FCSTD DOCUMENT  (FreeCAD 0.18R4 (GitTag))
Label: butelka bok
License: All rights reserved
LicenseURL: http://en.wikipedia.org/wiki/All_rights_reserved
objects: Sketcher::SketchObject×2, PartDesign::Body×1, Part::MultiFuse×1
note: 4 computed .brp shape members not serialized (recipe doc carries the construction recipe); baked Part::Feature solids carry a one-line shape summary decoded from their .brp

FEATURE [Sketcher::SketchObject] Sketch001
  AttachmentOffset = pos=(0,0,0) rot=(0,0,1;-0.331801rad)
  MapMode = 5
  Placement = pos=(0,0,0) rot=(0,0,1;5.95138rad)
  Support = -> [XY_Plane]
  sketch-geometry (153):
    g0: LineSegment StartX=0 StartY=0 StartZ=0 EndX=0 EndY=25 EndZ=0
    g1: LineSegment StartX=0 StartY=25 StartZ=0 EndX=-3.65 EndY=25 EndZ=0
    g2: LineSegment StartX=-3.65 StartY=25 StartZ=0 EndX=-3.65 EndY=28 EndZ=0
    g3: LineSegment StartX=-3.65 StartY=28 StartZ=0 EndX=0 EndY=28 EndZ=0
    g4: LineSegment StartX=0 StartY=28 StartZ=0 EndX=0 EndY=31 EndZ=0
    g5: LineSegment StartX=0 StartY=31 StartZ=0 EndX=-3.65 EndY=31 EndZ=0
    g6: LineSegment StartX=-3.65 StartY=31 StartZ=0 EndX=-3.65 EndY=34 EndZ=0
    g7: LineSegment StartX=-3.65 StartY=34 StartZ=0 EndX=0 EndY=34 EndZ=0
    g8: LineSegment StartX=0 StartY=34 StartZ=0 EndX=0 EndY=37 EndZ=0
    g9: LineSegment StartX=0 StartY=37 StartZ=0 EndX=-3.65 EndY=37 EndZ=0
    g10: LineSegment StartX=-3.65 StartY=37 StartZ=0 EndX=-3.65 EndY=40 EndZ=0
    g11: LineSegment StartX=-3.65 StartY=40 StartZ=0 EndX=0 EndY=40 EndZ=0
    g12: LineSegment StartX=0 StartY=40 StartZ=0 EndX=0 EndY=43 EndZ=0
    g13: LineSegment StartX=0 StartY=43 StartZ=0 EndX=-3.65 EndY=43 EndZ=0
    g14: LineSegment StartX=-3.65 StartY=43 StartZ=0 EndX=-3.65 EndY=46 EndZ=0
    g15: LineSegment StartX=-3.65 StartY=46 StartZ=0 EndX=0 EndY=46 EndZ=0
    g16: LineSegment StartX=0 StartY=46 StartZ=0 EndX=0 EndY=49 EndZ=0
    g17: LineSegment StartX=0 StartY=49 StartZ=0 EndX=-3.65 EndY=49 EndZ=0
    g18: LineSegment StartX=-3.65 StartY=49 StartZ=0 EndX=-3.65 EndY=52 EndZ=0
    g19: LineSegment StartX=-3.65 StartY=52 StartZ=0 EndX=0 EndY=52 EndZ=0
    g20: LineSegment StartX=0 StartY=52 StartZ=0 EndX=0 EndY=55 EndZ=0
    g21: LineSegment StartX=0 StartY=55 StartZ=0 EndX=-3.65 EndY=55 EndZ=0
    g22: LineSegment StartX=-3.65 StartY=55 StartZ=0 EndX=-3.65 EndY=58 EndZ=0
    g23: LineSegment StartX=-3.65 StartY=58 StartZ=0 EndX=0 EndY=58 EndZ=0
    g24: LineSegment StartX=0 StartY=58 StartZ=0 EndX=0 EndY=61 EndZ=0
    g25: LineSegment StartX=0 StartY=61 StartZ=0 EndX=-3.65 EndY=61 EndZ=0
    g26: LineSegment StartX=-3.65 StartY=61 StartZ=0 EndX=-3.65 EndY=64 EndZ=0
    g27: LineSegment StartX=-3.65 StartY=64 StartZ=0 EndX=0 EndY=64 EndZ=0
    g28: LineSegment StartX=0 StartY=64 StartZ=0 EndX=0 EndY=67 EndZ=0
    g29: LineSegment StartX=0 StartY=67 StartZ=0 EndX=-3.65 EndY=67 EndZ=0
    g30: LineSegment StartX=-3.65 StartY=67 StartZ=0 EndX=-3.65 EndY=70 EndZ=0
    g31: LineSegment StartX=-3.65 StartY=70 StartZ=0 EndX=0 EndY=70 EndZ=0
    g32: LineSegment StartX=0 StartY=70 StartZ=0 EndX=0 EndY=73 EndZ=0
    g33: LineSegment StartX=0 StartY=73 StartZ=0 EndX=-3.65 EndY=73 EndZ=0
    g34: LineSegment StartX=-3.65 StartY=73 StartZ=0 EndX=-3.65 EndY=76 EndZ=0
    g35: LineSegment StartX=-3.65 StartY=76 StartZ=0 EndX=0 EndY=76 EndZ=0
    g36: LineSegment StartX=0 StartY=76 StartZ=0 EndX=0 EndY=79 EndZ=0
    g37: LineSegment StartX=0 StartY=79 StartZ=0 EndX=-3.65 EndY=79 EndZ=0
    g38: LineSegment StartX=-3.65 StartY=79 StartZ=0 EndX=-3.65 EndY=82 EndZ=0
    g39: LineSegment StartX=-3.65 StartY=82 StartZ=0 EndX=0 EndY=82 EndZ=0
    g40: LineSegment StartX=0 StartY=82 StartZ=0 EndX=0 EndY=85 EndZ=0
    g41: LineSegment StartX=0 StartY=85 StartZ=0 EndX=-3.65 EndY=85 EndZ=0
    g42: LineSegment StartX=-3.65 StartY=85 StartZ=0 EndX=-3.65 EndY=88 EndZ=0
    g43: LineSegment StartX=-3.65 StartY=88 StartZ=0 EndX=0 EndY=88 EndZ=0
    g44: LineSegment StartX=0 StartY=88 StartZ=0 EndX=0 EndY=91 EndZ=0
    g45: LineSegment StartX=0 StartY=91 StartZ=0 EndX=-3.65 EndY=91 EndZ=0
    g46: LineSegment StartX=-3.65 StartY=91 StartZ=0 EndX=-3.65 EndY=94 EndZ=0
    g47: LineSegment StartX=-3.65 StartY=94 StartZ=0 EndX=0 EndY=94 EndZ=0
    g48: LineSegment StartX=0 StartY=94 StartZ=0 EndX=0 EndY=97 EndZ=0
    g49: LineSegment StartX=0 StartY=97 StartZ=0 EndX=-3.65 EndY=97 EndZ=0
    g50: LineSegment StartX=-3.65 StartY=97 StartZ=0 EndX=-3.65 EndY=100 EndZ=0
    g51: LineSegment StartX=-3.65 StartY=100 StartZ=0 EndX=0 EndY=100 EndZ=0
    g52: LineSegment StartX=0 StartY=100 StartZ=0 EndX=0 EndY=103 EndZ=0
    g53: LineSegment StartX=0 StartY=103 StartZ=0 EndX=-3.65 EndY=103 EndZ=0
    g54: LineSegment StartX=-3.65 StartY=103 StartZ=0 EndX=-3.65 EndY=106 EndZ=0
    g55: LineSegment StartX=-3.65 StartY=106 StartZ=0 EndX=0 EndY=106 EndZ=0
    g56: LineSegment StartX=0 StartY=106 StartZ=0 EndX=0 EndY=109 EndZ=0
    g57: LineSegment StartX=0 StartY=109 StartZ=0 EndX=-3.65 EndY=109 EndZ=0
    g58: LineSegment StartX=-3.65 StartY=109 StartZ=0 EndX=-3.65 EndY=112 EndZ=0
    g59: LineSegment StartX=-3.65 StartY=112 StartZ=0 EndX=0 EndY=112 EndZ=0
    g60: LineSegment StartX=0 StartY=112 StartZ=0 EndX=0 EndY=115 EndZ=0
    g61: LineSegment StartX=0 StartY=115 StartZ=0 EndX=-3.65 EndY=115 EndZ=0
    g62: LineSegment StartX=-3.65 StartY=115 StartZ=0 EndX=-3.65 EndY=118 EndZ=0
    g63: LineSegment StartX=-3.65 StartY=118 StartZ=0 EndX=0 EndY=118 EndZ=0
    g64: LineSegment StartX=0 StartY=118 StartZ=0 EndX=0 EndY=121 EndZ=0
    g65: LineSegment StartX=0 StartY=121 StartZ=0 EndX=-3.65 EndY=121 EndZ=0
    g66: LineSegment StartX=-3.65 StartY=121 StartZ=0 EndX=-3.65 EndY=124 EndZ=0
    g67: LineSegment StartX=-3.65 StartY=124 StartZ=0 EndX=0 EndY=124 EndZ=0
    g68: LineSegment StartX=0 StartY=124 StartZ=0 EndX=0 EndY=127 EndZ=0
    g69: LineSegment StartX=0 StartY=127 StartZ=0 EndX=-3.65 EndY=127 EndZ=0
    g70: LineSegment StartX=-3.65 StartY=127 StartZ=0 EndX=-3.65 EndY=130 EndZ=0
    g71: LineSegment StartX=-3.65 StartY=130 StartZ=0 EndX=0 EndY=130 EndZ=0
    g72: LineSegment StartX=0 StartY=130 StartZ=0 EndX=0 EndY=133 EndZ=0
    g73: LineSegment StartX=0 StartY=133 StartZ=0 EndX=-3.65 EndY=133 EndZ=0
    g74: LineSegment StartX=-3.65 StartY=133 StartZ=0 EndX=-3.65 EndY=136 EndZ=0
    g75: LineSegment StartX=-3.65 StartY=136 StartZ=0 EndX=0 EndY=136 EndZ=0
    g76: LineSegment StartX=0 StartY=136 StartZ=0 EndX=0 EndY=139 EndZ=0
    g77: LineSegment StartX=0 StartY=139 StartZ=0 EndX=-3.65 EndY=139 EndZ=0
    g78: LineSegment StartX=-3.65 StartY=139 StartZ=0 EndX=-3.65 EndY=142 EndZ=0
    g79: LineSegment StartX=-3.65 StartY=142 StartZ=0 EndX=0 EndY=142 EndZ=0
    g80: LineSegment StartX=0 StartY=142 StartZ=0 EndX=0 EndY=145 EndZ=0
    g81: LineSegment StartX=0 StartY=145 StartZ=0 EndX=-3.65 EndY=145 EndZ=0
    g82: LineSegment StartX=-3.65 StartY=145 StartZ=0 EndX=-3.65 EndY=148 EndZ=0
    g83: LineSegment StartX=-3.65 StartY=148 StartZ=0 EndX=0 EndY=148 EndZ=0
    g84: LineSegment StartX=0 StartY=148 StartZ=0 EndX=0 EndY=151 EndZ=0
    g85: LineSegment StartX=0 StartY=151 StartZ=0 EndX=-3.65 EndY=151 EndZ=0
    g86: LineSegment StartX=-3.65 StartY=151 StartZ=0 EndX=-3.65 EndY=154 EndZ=0
    g87: LineSegment StartX=-3.65 StartY=154 StartZ=0 EndX=0 EndY=154 EndZ=0
    g88: LineSegment StartX=0 StartY=154 StartZ=0 EndX=0 EndY=157 EndZ=0
    g89: LineSegment StartX=0 StartY=157 StartZ=0 EndX=-3.65 EndY=157 EndZ=0
    g90: LineSegment StartX=-3.65 StartY=157 StartZ=0 EndX=-3.65 EndY=160 EndZ=0
    g91: LineSegment StartX=-3.65 StartY=160 StartZ=0 EndX=0 EndY=160 EndZ=0
    g92: LineSegment StartX=0 StartY=160 StartZ=0 EndX=0 EndY=163 EndZ=0
    g93: LineSegment StartX=0 StartY=163 StartZ=0 EndX=-3.65 EndY=163 EndZ=0
    g94: LineSegment StartX=-3.65 StartY=163 StartZ=0 EndX=-3.65 EndY=166 EndZ=0
    g95: LineSegment StartX=-3.65 StartY=166 StartZ=0 EndX=0 EndY=166 EndZ=0
    g96: LineSegment StartX=0 StartY=166 StartZ=0 EndX=0 EndY=169 EndZ=0
    g97: LineSegment StartX=0 StartY=169 StartZ=0 EndX=-3.65 EndY=169 EndZ=0
    g98: LineSegment StartX=-3.65 StartY=169 StartZ=0 EndX=-3.65 EndY=172 EndZ=0
    g99: LineSegment StartX=-3.65 StartY=172 StartZ=0 EndX=0 EndY=172 EndZ=0
    g100: LineSegment StartX=0 StartY=172 StartZ=0 EndX=0 EndY=175 EndZ=0
    g101: LineSegment StartX=0 StartY=175 StartZ=0 EndX=-3.65 EndY=175 EndZ=0
    g102: LineSegment StartX=-3.65 StartY=175 StartZ=0 EndX=-3.65 EndY=178 EndZ=0
    g103: LineSegment StartX=-3.65 StartY=178 StartZ=0 EndX=0 EndY=178 EndZ=0
    g104: LineSegment StartX=0 StartY=178 StartZ=0 EndX=0 EndY=181 EndZ=0
    g105: LineSegment StartX=0 StartY=181 StartZ=0 EndX=-3.65 EndY=181 EndZ=0
    g106: LineSegment StartX=-3.65 StartY=181 StartZ=0 EndX=-3.65 EndY=184 EndZ=0
    g107: LineSegment StartX=-3.65 StartY=184 StartZ=0 EndX=0 EndY=184 EndZ=0
    g108: LineSegment StartX=0 StartY=184 StartZ=0 EndX=0 EndY=187 EndZ=0
    g109: LineSegment StartX=0 StartY=187 StartZ=0 EndX=-3.65 EndY=187 EndZ=0
    g110: LineSegment StartX=-3.65 StartY=187 StartZ=0 EndX=-3.65 EndY=190 EndZ=0
    g111: LineSegment StartX=-3.65 StartY=190 StartZ=0 EndX=0 EndY=190 EndZ=0
    g112: LineSegment StartX=0 StartY=190 StartZ=0 EndX=0 EndY=193 EndZ=0
    g113: LineSegment StartX=0 StartY=193 StartZ=0 EndX=-3.65 EndY=193 EndZ=0
    g114: LineSegment StartX=-3.65 StartY=193 StartZ=0 EndX=-3.65 EndY=196 EndZ=0
    g115: LineSegment StartX=-3.65 StartY=196 StartZ=0 EndX=0 EndY=196 EndZ=0
    g116: LineSegment StartX=0 StartY=196 StartZ=0 EndX=0 EndY=199 EndZ=0
    g117: LineSegment StartX=0 StartY=199 StartZ=0 EndX=-3.65 EndY=199 EndZ=0
    g118: LineSegment StartX=-3.65 StartY=199 StartZ=0 EndX=-3.65 EndY=202 EndZ=0
    g119: LineSegment StartX=-3.65 StartY=202 StartZ=0 EndX=0 EndY=202 EndZ=0
    g120: LineSegment StartX=0 StartY=202 StartZ=0 EndX=0 EndY=205 EndZ=0
    g121: LineSegment StartX=0 StartY=205 StartZ=0 EndX=-3.65 EndY=205 EndZ=0
    g122: LineSegment StartX=-3.65 StartY=205 StartZ=0 EndX=-3.65 EndY=208 EndZ=0
    g123: LineSegment StartX=-3.65 StartY=208 StartZ=0 EndX=0 EndY=208 EndZ=0
    g124: LineSegment StartX=0 StartY=208 StartZ=0 EndX=0 EndY=211 EndZ=0
    g125: LineSegment StartX=0 StartY=211 StartZ=0 EndX=-3.65 EndY=211 EndZ=0
    g126: LineSegment StartX=-3.65 StartY=211 StartZ=0 EndX=-3.65 EndY=214 EndZ=0
    g127: LineSegment StartX=-3.65 StartY=214 StartZ=0 EndX=0 EndY=214 EndZ=0
    g128: LineSegment StartX=0 StartY=214 StartZ=0 EndX=0 EndY=217 EndZ=0
    g129: LineSegment StartX=0 StartY=217 StartZ=0 EndX=-3.65 EndY=217 EndZ=0
    g130: LineSegment StartX=-3.65 StartY=217 StartZ=0 EndX=-3.65 EndY=220 EndZ=0
    g131: LineSegment StartX=-3.65 StartY=220 StartZ=0 EndX=0 EndY=220 EndZ=0
    g132: LineSegment StartX=0 StartY=220 StartZ=0 EndX=0 EndY=223 EndZ=0
    g133: LineSegment StartX=0 StartY=223 StartZ=0 EndX=-3.65 EndY=223 EndZ=0
    g134: LineSegment StartX=-3.65 StartY=223 StartZ=0 EndX=-3.65 EndY=226 EndZ=0
    g135: LineSegment StartX=-3.65 StartY=226 StartZ=0 EndX=0 EndY=226 EndZ=0
    g136: LineSegment StartX=0 StartY=226 StartZ=0 EndX=0 EndY=229 EndZ=0
    g137: LineSegment StartX=0 StartY=229 StartZ=0 EndX=-3.65 EndY=229 EndZ=0
    g138: LineSegment StartX=-3.65 StartY=229 StartZ=0 EndX=-3.65 EndY=232 EndZ=0
    g139: LineSegment StartX=-3.65 StartY=232 StartZ=0 EndX=0 EndY=232 EndZ=0
    g140: LineSegment StartX=0 StartY=232 StartZ=0 EndX=0 EndY=235 EndZ=0
    g141: LineSegment StartX=0 StartY=235 StartZ=0 EndX=-3.65 EndY=235 EndZ=0
    g142: LineSegment StartX=-3.65 StartY=235 StartZ=0 EndX=-3.65 EndY=238 EndZ=0
    g143: LineSegment StartX=-3.65 StartY=238 StartZ=0 EndX=0 EndY=238 EndZ=0
    g144: LineSegment StartX=0 StartY=238 StartZ=0 EndX=0 EndY=241 EndZ=0
    g145: LineSegment StartX=0 StartY=241 StartZ=0 EndX=-3.65 EndY=241 EndZ=0
    g146: LineSegment StartX=-3.65 StartY=241 StartZ=0 EndX=-3.65 EndY=244 EndZ=0
    g147: LineSegment StartX=-3.65 StartY=244 StartZ=0 EndX=0 EndY=244 EndZ=0
    g148: LineSegment StartX=0 StartY=244 StartZ=0 EndX=0 EndY=247 EndZ=0
    g149: LineSegment StartX=0 StartY=247 StartZ=0 EndX=-3.65 EndY=247 EndZ=0
    g150: LineSegment StartX=-3.65 StartY=247 StartZ=0 EndX=-3.65 EndY=250 EndZ=0
    g151: LineSegment StartX=-3.65 StartY=250 StartZ=0 EndX=0 EndY=250 EndZ=0
    g152: LineSegment StartX=0 StartY=250 StartZ=0 EndX=0 EndY=275 EndZ=0
FEATURE [Sketcher::SketchObject] Sketch
  MapMode = 5
  Support = -> [XY_Plane]
  sketch-geometry (154):
    g0: LineSegment StartX=0 StartY=0 StartZ=0 EndX=89.58 EndY=0 EndZ=0
    g1: LineSegment StartX=89.58 StartY=0 StartZ=0 EndX=89.58 EndY=17.5 EndZ=0
    g2: LineSegment StartX=89.58 StartY=17.5 StartZ=0 EndX=93.23 EndY=17.5 EndZ=0
    g3: LineSegment StartX=93.23 StartY=17.5 StartZ=0 EndX=93.23 EndY=20.5 EndZ=0
    g4: LineSegment StartX=93.23 StartY=20.5 StartZ=0 EndX=89.58 EndY=20.5 EndZ=0
    g5: LineSegment StartX=89.58 StartY=20.5 StartZ=0 EndX=89.58 EndY=23.5 EndZ=0
    g6: LineSegment StartX=89.58 StartY=23.5 StartZ=0 EndX=93.23 EndY=23.5 EndZ=0
    g7: LineSegment StartX=93.23 StartY=23.5 StartZ=0 EndX=93.23 EndY=26.5 EndZ=0
    g8: LineSegment StartX=93.23 StartY=26.5 StartZ=0 EndX=89.58 EndY=26.5 EndZ=0
    g9: LineSegment StartX=89.58 StartY=26.5 StartZ=0 EndX=89.58 EndY=29.5 EndZ=0
    g10: LineSegment StartX=89.58 StartY=29.5 StartZ=0 EndX=93.23 EndY=29.5 EndZ=0
    g11: LineSegment StartX=93.23 StartY=29.5 StartZ=0 EndX=93.23 EndY=32.5 EndZ=0
    g12: LineSegment StartX=93.23 StartY=32.5 StartZ=0 EndX=89.58 EndY=32.5 EndZ=0
    g13: LineSegment StartX=89.58 StartY=32.5 StartZ=0 EndX=89.58 EndY=35.5 EndZ=0
    g14: LineSegment StartX=89.58 StartY=35.5 StartZ=0 EndX=93.23 EndY=35.5 EndZ=0
    g15: LineSegment StartX=93.23 StartY=35.5 StartZ=0 EndX=93.23 EndY=38.5 EndZ=0
    g16: LineSegment StartX=93.23 StartY=38.5 StartZ=0 EndX=89.58 EndY=38.5 EndZ=0
    g17: LineSegment StartX=89.58 StartY=38.5 StartZ=0 EndX=89.58 EndY=41.5 EndZ=0
    g18: LineSegment StartX=89.58 StartY=41.5 StartZ=0 EndX=93.23 EndY=41.5 EndZ=0
    g19: LineSegment StartX=93.23 StartY=41.5 StartZ=0 EndX=93.23 EndY=44.5 EndZ=0
    g20: LineSegment StartX=93.23 StartY=44.5 StartZ=0 EndX=89.58 EndY=44.5 EndZ=0
    g21: LineSegment StartX=89.58 StartY=44.5 StartZ=0 EndX=89.58 EndY=47.5 EndZ=0
    g22: LineSegment StartX=89.58 StartY=47.5 StartZ=0 EndX=93.23 EndY=47.5 EndZ=0
    g23: LineSegment StartX=93.23 StartY=47.5 StartZ=0 EndX=93.23 EndY=50.5 EndZ=0
    g24: LineSegment StartX=93.23 StartY=50.5 StartZ=0 EndX=89.58 EndY=50.5 EndZ=0
    g25: LineSegment StartX=89.58 StartY=50.5 StartZ=0 EndX=89.58 EndY=53.5 EndZ=0
    g26: LineSegment StartX=89.58 StartY=53.5 StartZ=0 EndX=93.23 EndY=53.5 EndZ=0
    g27: LineSegment StartX=93.23 StartY=53.5 StartZ=0 EndX=93.23 EndY=56.5 EndZ=0
    g28: LineSegment StartX=93.23 StartY=56.5 StartZ=0 EndX=89.58 EndY=56.5 EndZ=0
    g29: LineSegment StartX=89.58 StartY=56.5 StartZ=0 EndX=89.58 EndY=59.5 EndZ=0
    g30: LineSegment StartX=89.58 StartY=59.5 StartZ=0 EndX=93.23 EndY=59.5 EndZ=0
    g31: LineSegment StartX=93.23 StartY=59.5 StartZ=0 EndX=93.23 EndY=62.5 EndZ=0
    g32: LineSegment StartX=93.23 StartY=62.5 StartZ=0 EndX=89.58 EndY=62.5 EndZ=0
    g33: LineSegment StartX=89.58 StartY=62.5 StartZ=0 EndX=89.58 EndY=65.5 EndZ=0
    g34: LineSegment StartX=89.58 StartY=65.5 StartZ=0 EndX=93.23 EndY=65.5 EndZ=0
    g35: LineSegment StartX=93.23 StartY=65.5 StartZ=0 EndX=93.23 EndY=68.5 EndZ=0
    g36: LineSegment StartX=93.23 StartY=68.5 StartZ=0 EndX=89.58 EndY=68.5 EndZ=0
    g37: LineSegment StartX=89.58 StartY=68.5 StartZ=0 EndX=89.58 EndY=71.5 EndZ=0
    g38: LineSegment StartX=89.58 StartY=71.5 StartZ=0 EndX=93.23 EndY=71.5 EndZ=0
    g39: LineSegment StartX=93.23 StartY=71.5 StartZ=0 EndX=93.23 EndY=74.5 EndZ=0
    g40: LineSegment StartX=93.23 StartY=74.5 StartZ=0 EndX=89.58 EndY=74.5 EndZ=0
    g41: LineSegment StartX=89.58 StartY=74.5 StartZ=0 EndX=89.58 EndY=77.5 EndZ=0
    g42: LineSegment StartX=89.58 StartY=77.5 StartZ=0 EndX=93.23 EndY=77.5 EndZ=0
    g43: LineSegment StartX=93.23 StartY=77.5 StartZ=0 EndX=93.23 EndY=80.5 EndZ=0
    g44: LineSegment StartX=93.23 StartY=80.5 StartZ=0 EndX=89.58 EndY=80.5 EndZ=0
    g45: LineSegment StartX=89.58 StartY=80.5 StartZ=0 EndX=89.58 EndY=83.5 EndZ=0
    g46: LineSegment StartX=89.58 StartY=83.5 StartZ=0 EndX=93.23 EndY=83.5 EndZ=0
    g47: LineSegment StartX=93.23 StartY=83.5 StartZ=0 EndX=93.23 EndY=86.5 EndZ=0
    g48: LineSegment StartX=93.23 StartY=86.5 StartZ=0 EndX=89.58 EndY=86.5 EndZ=0
    g49: LineSegment StartX=89.58 StartY=86.5 StartZ=0 EndX=89.58 EndY=89.5 EndZ=0
    g50: LineSegment StartX=89.58 StartY=89.5 StartZ=0 EndX=93.23 EndY=89.5 EndZ=0
    g51: LineSegment StartX=93.23 StartY=89.5 StartZ=0 EndX=93.23 EndY=92.5 EndZ=0
    g52: LineSegment StartX=93.23 StartY=92.5 StartZ=0 EndX=89.58 EndY=92.5 EndZ=0
    g53: LineSegment StartX=89.58 StartY=92.5 StartZ=0 EndX=89.58 EndY=95.5 EndZ=0
    g54: LineSegment StartX=89.58 StartY=95.5 StartZ=0 EndX=93.23 EndY=95.5 EndZ=0
    g55: LineSegment StartX=93.23 StartY=95.5 StartZ=0 EndX=93.23 EndY=98.5 EndZ=0
    g56: LineSegment StartX=93.23 StartY=98.5 StartZ=0 EndX=89.58 EndY=98.5 EndZ=0
    g57: LineSegment StartX=89.58 StartY=98.5 StartZ=0 EndX=89.58 EndY=101.5 EndZ=0
    g58: LineSegment StartX=89.58 StartY=101.5 StartZ=0 EndX=93.23 EndY=101.5 EndZ=0
    g59: LineSegment StartX=93.23 StartY=101.5 StartZ=0 EndX=93.23 EndY=104.5 EndZ=0
    g60: LineSegment StartX=93.23 StartY=104.5 StartZ=0 EndX=89.58 EndY=104.5 EndZ=0
    g61: LineSegment StartX=89.58 StartY=104.5 StartZ=0 EndX=89.58 EndY=107.5 EndZ=0
    g62: LineSegment StartX=89.58 StartY=107.5 StartZ=0 EndX=93.23 EndY=107.5 EndZ=0
    g63: LineSegment StartX=93.23 StartY=107.5 StartZ=0 EndX=93.23 EndY=110.5 EndZ=0
    g64: LineSegment StartX=93.23 StartY=110.5 StartZ=0 EndX=89.58 EndY=110.5 EndZ=0
    g65: LineSegment StartX=89.58 StartY=110.5 StartZ=0 EndX=89.58 EndY=113.5 EndZ=0
    g66: LineSegment StartX=89.58 StartY=113.5 StartZ=0 EndX=93.23 EndY=113.5 EndZ=0
    g67: LineSegment StartX=93.23 StartY=113.5 StartZ=0 EndX=93.23 EndY=116.5 EndZ=0
    g68: LineSegment StartX=93.23 StartY=116.5 StartZ=0 EndX=89.58 EndY=116.5 EndZ=0
    g69: LineSegment StartX=89.58 StartY=116.5 StartZ=0 EndX=89.58 EndY=119.5 EndZ=0
    g70: LineSegment StartX=89.58 StartY=119.5 StartZ=0 EndX=93.23 EndY=119.5 EndZ=0
    g71: LineSegment StartX=93.23 StartY=119.5 StartZ=0 EndX=93.23 EndY=122.5 EndZ=0
    g72: LineSegment StartX=93.23 StartY=122.5 StartZ=0 EndX=89.58 EndY=122.5 EndZ=0
    g73: LineSegment StartX=89.58 StartY=122.5 StartZ=0 EndX=89.58 EndY=125.5 EndZ=0
    g74: LineSegment StartX=89.58 StartY=125.5 StartZ=0 EndX=93.23 EndY=125.5 EndZ=0
    g75: LineSegment StartX=93.23 StartY=125.5 StartZ=0 EndX=93.23 EndY=128.5 EndZ=0
    g76: LineSegment StartX=93.23 StartY=128.5 StartZ=0 EndX=89.58 EndY=128.5 EndZ=0
    g77: LineSegment StartX=89.58 StartY=128.5 StartZ=0 EndX=89.58 EndY=131.5 EndZ=0
    g78: LineSegment StartX=89.58 StartY=131.5 StartZ=0 EndX=93.23 EndY=131.5 EndZ=0
    g79: LineSegment StartX=93.23 StartY=131.5 StartZ=0 EndX=93.23 EndY=134.5 EndZ=0
    g80: LineSegment StartX=93.23 StartY=134.5 StartZ=0 EndX=89.58 EndY=134.5 EndZ=0
    g81: LineSegment StartX=89.58 StartY=134.5 StartZ=0 EndX=89.58 EndY=137.5 EndZ=0
    g82: LineSegment StartX=89.58 StartY=137.5 StartZ=0 EndX=93.23 EndY=137.5 EndZ=0
    g83: LineSegment StartX=93.23 StartY=137.5 StartZ=0 EndX=93.23 EndY=140.5 EndZ=0
    g84: LineSegment StartX=93.23 StartY=140.5 StartZ=0 EndX=89.58 EndY=140.5 EndZ=0
    g85: LineSegment StartX=89.58 StartY=140.5 StartZ=0 EndX=89.58 EndY=143.5 EndZ=0
    g86: LineSegment StartX=89.58 StartY=143.5 StartZ=0 EndX=93.23 EndY=143.5 EndZ=0
    g87: LineSegment StartX=93.23 StartY=143.5 StartZ=0 EndX=93.23 EndY=146.5 EndZ=0
    g88: LineSegment StartX=93.23 StartY=146.5 StartZ=0 EndX=89.58 EndY=146.5 EndZ=0
    g89: LineSegment StartX=89.58 StartY=146.5 StartZ=0 EndX=89.58 EndY=149.5 EndZ=0
    g90: LineSegment StartX=89.58 StartY=149.5 StartZ=0 EndX=93.23 EndY=149.5 EndZ=0
    g91: LineSegment StartX=93.23 StartY=149.5 StartZ=0 EndX=93.23 EndY=152.5 EndZ=0
    g92: LineSegment StartX=93.23 StartY=152.5 StartZ=0 EndX=89.58 EndY=152.5 EndZ=0
    g93: LineSegment StartX=89.58 StartY=152.5 StartZ=0 EndX=89.58 EndY=155.5 EndZ=0
    g94: LineSegment StartX=89.58 StartY=155.5 StartZ=0 EndX=93.23 EndY=155.5 EndZ=0
    g95: LineSegment StartX=93.23 StartY=155.5 StartZ=0 EndX=93.23 EndY=158.5 EndZ=0
    g96: LineSegment StartX=93.23 StartY=158.5 StartZ=0 EndX=89.58 EndY=158.5 EndZ=0
    g97: LineSegment StartX=89.58 StartY=158.5 StartZ=0 EndX=89.58 EndY=161.5 EndZ=0
    g98: LineSegment StartX=89.58 StartY=161.5 StartZ=0 EndX=93.23 EndY=161.5 EndZ=0
    g99: LineSegment StartX=93.23 StartY=161.5 StartZ=0 EndX=93.23 EndY=164.5 EndZ=0
    g100: LineSegment StartX=93.23 StartY=164.5 StartZ=0 EndX=89.58 EndY=164.5 EndZ=0
    g101: LineSegment StartX=89.58 StartY=164.5 StartZ=0 EndX=89.58 EndY=167.5 EndZ=0
    g102: LineSegment StartX=89.58 StartY=167.5 StartZ=0 EndX=93.23 EndY=167.5 EndZ=0
    g103: LineSegment StartX=93.23 StartY=167.5 StartZ=0 EndX=93.23 EndY=170.5 EndZ=0
    g104: LineSegment StartX=93.23 StartY=170.5 StartZ=0 EndX=89.58 EndY=170.5 EndZ=0
    g105: LineSegment StartX=89.58 StartY=170.5 StartZ=0 EndX=89.58 EndY=173.5 EndZ=0
    g106: LineSegment StartX=89.58 StartY=173.5 StartZ=0 EndX=93.23 EndY=173.5 EndZ=0
    g107: LineSegment StartX=93.23 StartY=173.5 StartZ=0 EndX=93.23 EndY=176.5 EndZ=0
    g108: LineSegment StartX=93.23 StartY=176.5 StartZ=0 EndX=89.58 EndY=176.5 EndZ=0
    g109: LineSegment StartX=89.58 StartY=176.5 StartZ=0 EndX=89.58 EndY=179.5 EndZ=0
    g110: LineSegment StartX=89.58 StartY=179.5 StartZ=0 EndX=93.23 EndY=179.5 EndZ=0
    g111: LineSegment StartX=93.23 StartY=179.5 StartZ=0 EndX=93.23 EndY=182.5 EndZ=0
    g112: LineSegment StartX=93.23 StartY=182.5 StartZ=0 EndX=89.58 EndY=182.5 EndZ=0
    g113: LineSegment StartX=89.58 StartY=182.5 StartZ=0 EndX=89.58 EndY=185.5 EndZ=0
    g114: LineSegment StartX=89.58 StartY=185.5 StartZ=0 EndX=93.23 EndY=185.5 EndZ=0
    g115: LineSegment StartX=93.23 StartY=185.5 StartZ=0 EndX=93.23 EndY=188.5 EndZ=0
    g116: LineSegment StartX=93.23 StartY=188.5 StartZ=0 EndX=89.58 EndY=188.5 EndZ=0
    g117: LineSegment StartX=89.58 StartY=188.5 StartZ=0 EndX=89.58 EndY=191.5 EndZ=0
    g118: LineSegment StartX=89.58 StartY=191.5 StartZ=0 EndX=93.23 EndY=191.5 EndZ=0
    g119: LineSegment StartX=93.23 StartY=191.5 StartZ=0 EndX=93.23 EndY=194.5 EndZ=0
    g120: LineSegment StartX=93.23 StartY=194.5 StartZ=0 EndX=89.58 EndY=194.5 EndZ=0
    g121: LineSegment StartX=89.58 StartY=194.5 StartZ=0 EndX=89.58 EndY=197.5 EndZ=0
    g122: LineSegment StartX=89.58 StartY=197.5 StartZ=0 EndX=93.23 EndY=197.5 EndZ=0
    g123: LineSegment StartX=93.23 StartY=197.5 StartZ=0 EndX=93.23 EndY=200.5 EndZ=0
    g124: LineSegment StartX=93.23 StartY=200.5 StartZ=0 EndX=89.58 EndY=200.5 EndZ=0
    g125: LineSegment StartX=89.58 StartY=200.5 StartZ=0 EndX=89.58 EndY=203.5 EndZ=0
    g126: LineSegment StartX=89.58 StartY=203.5 StartZ=0 EndX=93.23 EndY=203.5 EndZ=0
    g127: LineSegment StartX=93.23 StartY=203.5 StartZ=0 EndX=93.23 EndY=206.5 EndZ=0
    g128: LineSegment StartX=93.23 StartY=206.5 StartZ=0 EndX=89.58 EndY=206.5 EndZ=0
    g129: LineSegment StartX=89.58 StartY=206.5 StartZ=0 EndX=89.58 EndY=209.5 EndZ=0
    g130: LineSegment StartX=89.58 StartY=209.5 StartZ=0 EndX=93.23 EndY=209.5 EndZ=0
    g131: LineSegment StartX=93.23 StartY=209.5 StartZ=0 EndX=93.23 EndY=212.5 EndZ=0
    g132: LineSegment StartX=93.23 StartY=212.5 StartZ=0 EndX=89.58 EndY=212.5 EndZ=0
    g133: LineSegment StartX=89.58 StartY=212.5 StartZ=0 EndX=89.58 EndY=215.5 EndZ=0
    g134: LineSegment StartX=89.58 StartY=215.5 StartZ=0 EndX=93.23 EndY=215.5 EndZ=0
    g135: LineSegment StartX=93.23 StartY=215.5 StartZ=0 EndX=93.23 EndY=218.5 EndZ=0
    g136: LineSegment StartX=93.23 StartY=218.5 StartZ=0 EndX=89.58 EndY=218.5 EndZ=0
    g137: LineSegment StartX=89.58 StartY=218.5 StartZ=0 EndX=89.58 EndY=221.5 EndZ=0
    g138: LineSegment StartX=89.58 StartY=221.5 StartZ=0 EndX=93.23 EndY=221.5 EndZ=0
    g139: LineSegment StartX=93.23 StartY=221.5 StartZ=0 EndX=93.23 EndY=224.5 EndZ=0
    g140: LineSegment StartX=93.23 StartY=224.5 StartZ=0 EndX=89.58 EndY=224.5 EndZ=0
    g141: LineSegment StartX=89.58 StartY=224.5 StartZ=0 EndX=89.58 EndY=227.5 EndZ=0
    g142: LineSegment StartX=89.58 StartY=227.5 StartZ=0 EndX=93.23 EndY=227.5 EndZ=0
    g143: LineSegment StartX=93.23 StartY=227.5 StartZ=0 EndX=93.23 EndY=230.5 EndZ=0
    g144: LineSegment StartX=93.23 StartY=230.5 StartZ=0 EndX=89.58 EndY=230.5 EndZ=0
    g145: LineSegment StartX=89.58 StartY=230.5 StartZ=0 EndX=89.58 EndY=233.5 EndZ=0
    g146: LineSegment StartX=89.58 StartY=233.5 StartZ=0 EndX=93.23 EndY=233.5 EndZ=0
    g147: LineSegment StartX=93.23 StartY=233.5 StartZ=0 EndX=93.23 EndY=236.5 EndZ=0
    g148: LineSegment StartX=93.23 StartY=236.5 StartZ=0 EndX=89.58 EndY=236.5 EndZ=0
    g149: LineSegment StartX=89.58 StartY=236.5 StartZ=0 EndX=89.58 EndY=239.5 EndZ=0
    g150: LineSegment StartX=89.58 StartY=239.5 StartZ=0 EndX=93.23 EndY=239.5 EndZ=0
    g151: LineSegment StartX=93.23 StartY=239.5 StartZ=0 EndX=93.23 EndY=242.5 EndZ=0
    g152: LineSegment StartX=93.23 StartY=242.5 StartZ=0 EndX=89.58 EndY=242.5 EndZ=0
    g153: LineSegment StartX=89.58 StartY=242.5 StartZ=0 EndX=89.58 EndY=260 EndZ=0
FEATURE [PartDesign::Body] Body
  Group = -> [Sketch]
  Origin = -> Origin
FEATURE [Part::MultiFuse] Fusion
  Shapes = -> [Sketch,Sketch001]
